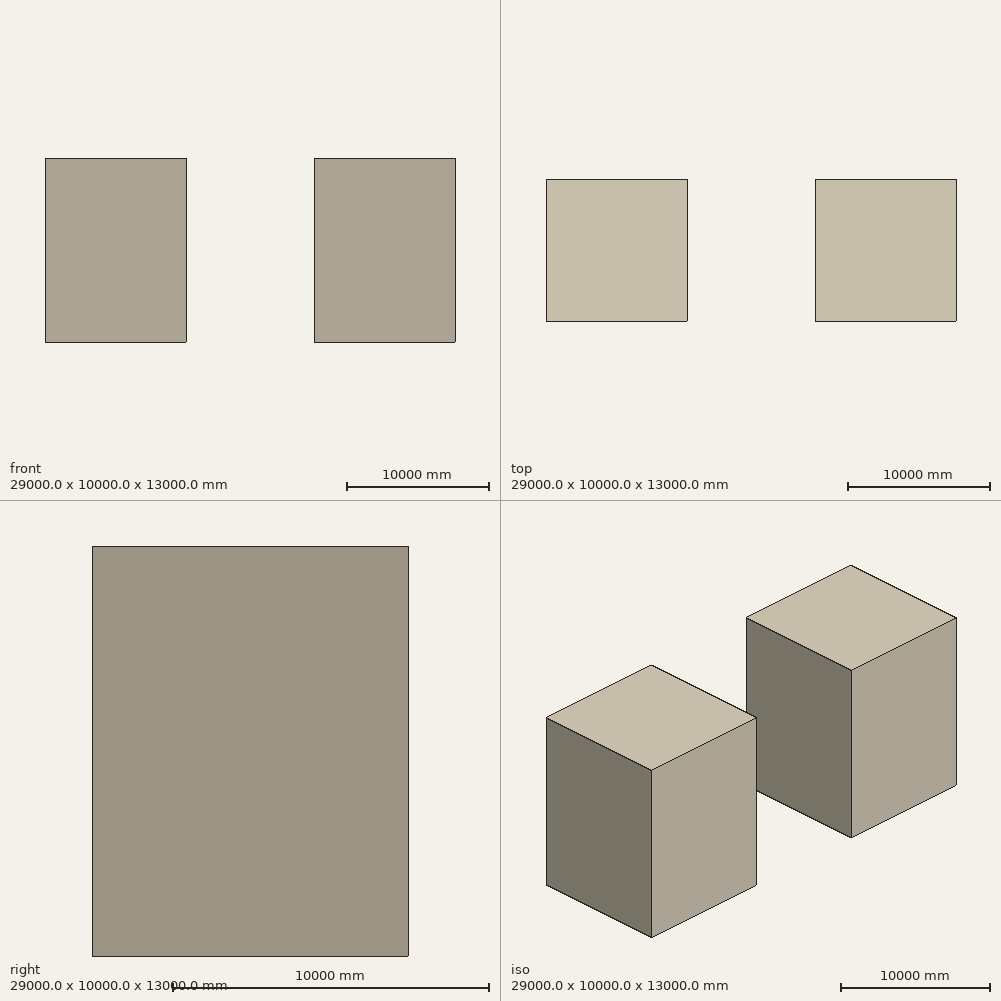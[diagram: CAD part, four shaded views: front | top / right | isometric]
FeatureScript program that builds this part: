
annotation { "Feature Type Name" : "Feature", "Feature Type Description" : "" }
export const myFeature = defineFeature(function(context is Context, id is Id, definition is map)
    precondition{}
    {
        {
            var Q0;
            Q0=qCreatedBy(makeId("Front.planeOp"),FACE);
            var sketch = newSketch(context, id + "F0", { "sketchPlane" : qUnion([Q0])});
            skLineSegment(sketch, "E0.bottom", {"start": v(-14500, 0) * mm, "end": v(-4500, 0) * mm});
            skLineSegment(sketch, "E0.top", {"start": v(-14500, 13000) * mm, "end": v(-4500, 13000) * mm});
            skLineSegment(sketch, "E0.left", {"start": v(-14500, 0) * mm, "end": v(-14500, 13000) * mm});
            skLineSegment(sketch, "E0.right", {"start": v(-4500, 0) * mm, "end": v(-4500, 13000) * mm});
            skLineSegment(sketch, "E1.bottom", {"start": v(4500, 0) * mm, "end": v(14500, 0) * mm});
            skLineSegment(sketch, "E1.top", {"start": v(4500, 13000) * mm, "end": v(14500, 13000) * mm});
            skLineSegment(sketch, "E1.left", {"start": v(4500, 0) * mm, "end": v(4500, 13000) * mm});
            skLineSegment(sketch, "E1.right", {"start": v(14500, 0) * mm, "end": v(14500, 13000) * mm});
            skSolve(sketch);
        }
        {
            var Q0;
            Q0 = qSketchRegion(id + "F0", true);
            extrude(context, id + "F1", {"entities" : qUnion([Q0]), "endBound" : BoundingType.SYMMETRIC, "depth" : 10000 * mm, "offsetDistance" : 25 * mm});
        }
    });
